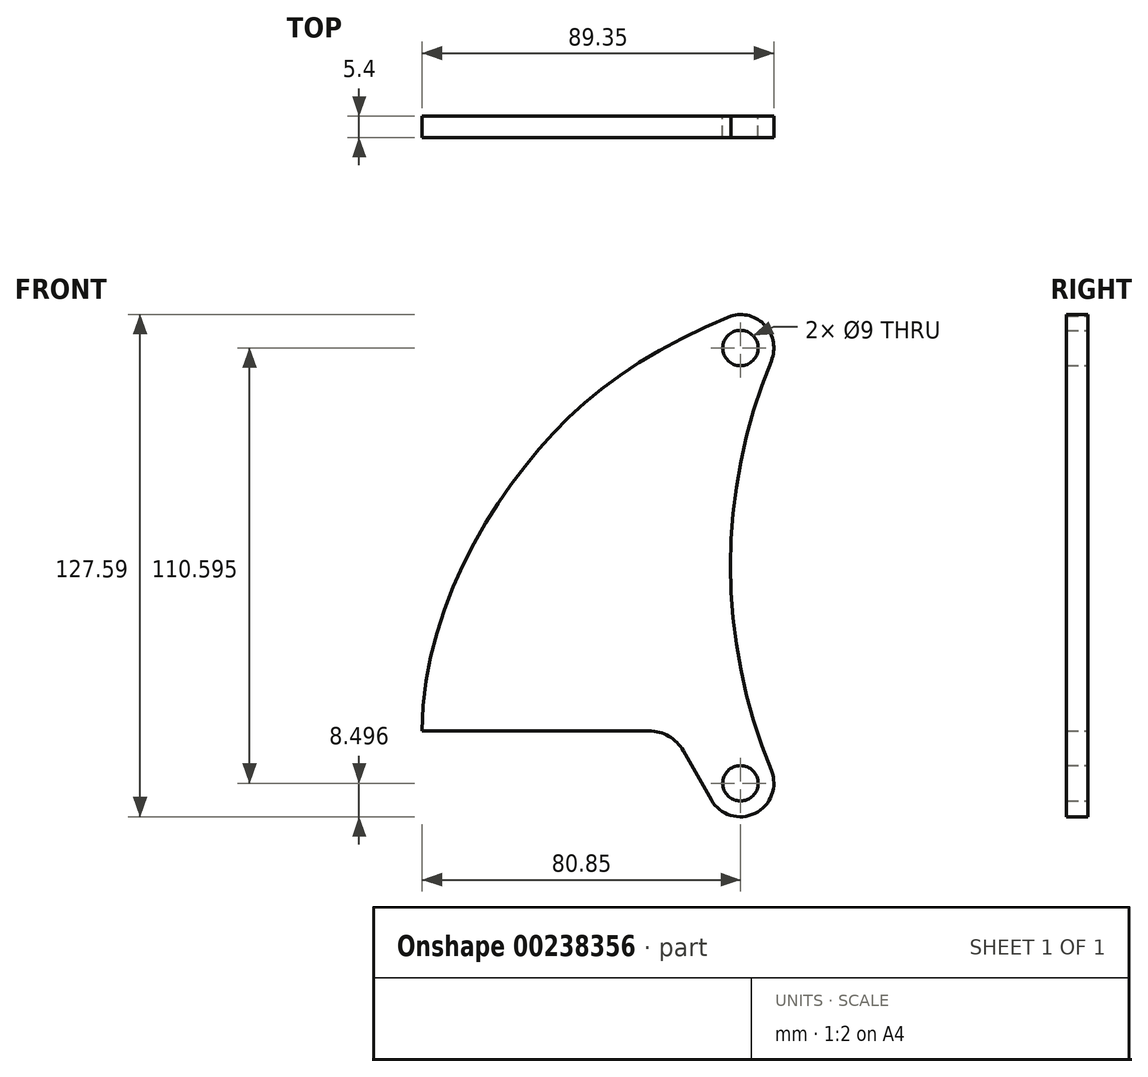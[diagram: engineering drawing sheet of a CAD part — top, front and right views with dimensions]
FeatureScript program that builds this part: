
annotation { "Feature Type Name" : "Feature", "Feature Type Description" : "" }
export const myFeature = defineFeature(function(context is Context, id is Id, definition is map)
    precondition{}
    {
        {
            var Q0;
            Q0=qCreatedBy(makeId("Front.planeOp"),FACE);
            var sketch = newSketch(context, id + "F0", { "sketchPlane" : qUnion([Q0])});
            skCircle(sketch, "E0", {"center": v(62.48, 2.53) * mm, "radius": 144.5 * mm, "construction": true});
            skCircle(sketch, "E1", {"center": v(117.78, 136.03) * mm, "radius": 4.5 * mm, "construction": true});
            skCircle(sketch, "E2.1.0", {"center": v(7.18, 136.03) * mm, "radius": 4.5 * mm, "construction": true});
            skCircle(sketch, "E2.2.0", {"center": v(-71.02, 57.83) * mm, "radius": 4.5 * mm});
            skCircle(sketch, "E2.3.0", {"center": v(-71.02, -52.76) * mm, "radius": 4.5 * mm});
            skCircle(sketch, "E2.4.0", {"center": v(7.18, -130.97) * mm, "radius": 4.5 * mm, "construction": true});
            skCircle(sketch, "E2.5.0", {"center": v(117.78, -130.97) * mm, "radius": 4.5 * mm, "construction": true});
            skCircle(sketch, "E2.6.0", {"center": v(195.98, -52.76) * mm, "radius": 4.5 * mm, "construction": true});
            skCircle(sketch, "E2.7.0", {"center": v(195.98, 57.83) * mm, "radius": 4.5 * mm, "construction": true});
            skLineSegment(sketch, "E3", {"start": v(62.48, 2.53) * mm, "end": v(62.48, 172.97) * mm, "construction": true});
            skLineSegment(sketch, "E4", {"start": v(62.48, 2.53) * mm, "end": v(117.78, 136.03) * mm, "construction": true});
            skArc(sketch, "E5.0", {"start": v(-63.17, -49.51) * mm, "mid": v(-73.52, 2.53) * mm, "end": v(-63.17, 54.58) * mm});
            skLineSegment(sketch, "E6", {"start": v(-151.87, -39.47) * mm, "end": v(-94.22, -39.47) * mm});
            skArc(sketch, "E7.0", {"start": v(-78.4, -56.99) * mm, "mid": v(-67.28, -60.4) * mm, "end": v(-63.17, -49.51) * mm});
            skArc(sketch, "E8.0", {"start": v(-63.17, 54.58) * mm, "mid": v(-64.7, 63.53) * mm, "end": v(-73.45, 65.98) * mm});
            skPoint(sketch, "E9", {"position": v(-66.87, -39.47) * mm});
            skFitSpline(sketch, "E10", {"points": [v(-151.87, -39.47) * mm, v(-127.04, 26.17) * mm, v(-73.45, 65.98) * mm], "startDerivative": vector(0.85, 147.98) * mm, "endDerivative": vector(153.73, 64.2) * mm});
            skLineSegment(sketch, "E11", {"start": v(-78.4, -56.99) * mm, "end": v(-85.54, -44.5) * mm});
            skPoint(sketch, "E12.visualSharp", {"position": v(-88.42, -39.47) * mm});
            skArc(sketch, "E12.filletArc", {"start": v(-85.54, -44.5) * mm, "mid": v(-89.2, -40.82) * mm, "end": v(-94.22, -39.47) * mm});
            skSolve(sketch);
        }
        {
            var Q0;
            Q0 = qSketchRegion(id + "F0", true);
            extrude(context, id + "F1", {"entities" : qUnion([Q0]), "depth" : 5.4 * mm});
        }
    });
